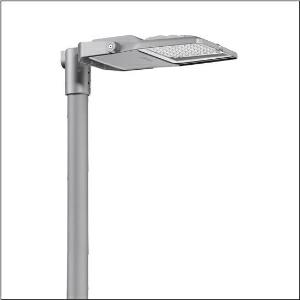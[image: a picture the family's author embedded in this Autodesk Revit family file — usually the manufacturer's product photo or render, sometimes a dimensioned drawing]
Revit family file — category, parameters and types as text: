
# Revit family: floodlight_fl_21_iq_mini___pl33t_5xa7771c4f3a_1d16
name_source: partatom
category: Lighting Fixtures
units: mm (PartAtom-declared; Revit-internal decimal feet)

## family parameters
Cut with Voids When Loaded = No
Host = Face
Light Source = No
Part Type = Normal
Room Calculation Point = No
Round Connector Dimension = Use Diameter
Shared = No

## types (1)
- --- (1 x LED, 12570 lm, 87.2 W, 4000K)
    Apparent Load = 87 VA
    CIE Flux Codes = 26 75 99 100 100
    Color Rendering = 70
    Color Temperature = 4000K
    Default Elevation = 1800 mm
    Description = Floodlight FL 21 iQ mini, floodlight, primary light control with lens, of PMMA, primary optical cover: protective disc, of toughened safety glass, transparent, light distribution: PL33T, light emission: direct distribution, installation type: surface-mounted, LED, High Power LED, rated luminous flux: 12.570lm, luminous efficacy: 144lm/W, light colour: 740, colour temperature: 4000K, control: Auto-Match, Temp-Guard, Lumen-Switch, Night-Set, Smart-Wire, Light-Fading, Desk-Remote (wireless, voltage-free reading and setting of iQ features in the workshop via application-optimized NFC function/RFID function), optimised constant luminous flux control (CLO 2.0), with terminal, 6-pole, mains connection: 220..240V, AC, 50/60Hz, start of lifetime: 87W, end of service life: 92W, reduction: 40W, luminaire housing, of diecast aluminium, powder-coated, Siteco® metallic grey (DB 702S), corrosivity category C5 mid according to DIN EN ISO 12944, sealing non-destructively replaceable, please order mast flange separately, mast bracket, of steel, galvanised, powder-coated, Siteco® metallic grey (DB 702S), protection rating (complete): IP66, insulation class (complete): insulation class II (safety insulation), certification: CE, ENEC, VDE, protection symbol: D, impact resistance: IK08, permissible operating ambient temperature: -40..+40°C, permissible operating ambient temperature for outdoor applications: -40..+50°C, standard: DIN EN 12944, LABS conformity tested according to VDMA 24364:2018-05, packaging unit: 1 piece

Light Distribution: PL33T
    Height = 70 mm
    Lamp = 1 x LED
    Lamp Light Flux = 12570 lm
    Lamp Power = 87.2 W
    Lamp count = 1
    Length = 485 mm
    Luminous efficacy = 144 lm/W
    Manufacturer = Siteco
    ModVariant = No
    Model = 5XA7771C4F3A
    Number of Poles = 1
    OnlyDefault = Yes
    Power Factor = 1
    Product Name = Floodlight FL 21 iQ mini | PL33T
    Product group = floodlight | pylon annexe
    ProductGroupID = 6200
    Protection Class = Protection class II
    Protection Degree = IP 66
    RLX_Detail_Level = 1
    RLX_Emergency_Light_Flux = 0 lm
    RLX_Emergency_Type = 0
    RLX_Emergency_Type_DB = No
    RlxData = <blob elided: 101225 chars, md5=c4cf1053>
    Socket = socket
    Standby Power = 0 W
    System Light Flux = 12570 lm
    System Power = 87 W
    Type Comments = factory setting: luminous flux: 100 % | dim-lin: 254 | 456 mA
    Type Image = l_1007125.jpg
    URL = http://relux.com
    VarID = @adj_082119
    Voltage = 0 V
    Weight = 0.00 kg
    Width = 337 mm

## geometry (parser evidence)
native form markers: Blend x4, Sweep x13
no freeform markers — native parametric forms only
